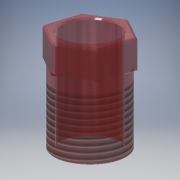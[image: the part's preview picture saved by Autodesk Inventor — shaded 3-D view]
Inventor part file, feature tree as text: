
AUTODESK INVENTOR PART (.ipt)
format: ipt  version: 2018 (Build 220112000, 112)  size: 318,464 bytes
history: native  units: mm
features: extrude x3, fillet x3, sketch x3, chamfer x1, thread x1
ambient origin geometry x8: Origin, YZ Plane, XZ Plane, XY Plane, X Axis, Y Axis, Z Axis, Center Point
bodies: Solid1 (feature_tree)
feature tree (11):
  extrude  "Extrusion1"  Depth=5.0mm TaperAngle=0.0deg
  extrude  "Extrusion2"  Depth=17.5mm TaperAngle=0.0deg
  extrude  "Extrusion3"  Depth=34.5mm TaperAngle=0.0deg
  chamfer  "Chamfer1"  Distance=0.25mm Angle=45.0deg
  thread  "Thread1"  [1 undecoded]
  fillet  "Fillet1"  Radius=0.5mm
  fillet  "Fillet2"  Radius=0.2mm
  fillet  "Fillet3"  Radius=0.2mm
  sketch  "Sketch1"  dims[d0=12.0mm d1=5.0mm d2=0.0mm]
  sketch  "Sketch2"  dims[d3=12.0mm d4=17.5mm d5=0.0mm]
  sketch  "Sketch3"  dims[d6=9.5mm d7=34.5mm d8=0.0mm d9=0.25mm d10=2.0mm d11=45.0deg d12=10.2mm d13=0.0mm d14=0.5mm d15=0.2mm d16=0.2mm]
note: 1 required parameter value undecoded (feature->parameter linkage not recoverable at this tier; creation-order binding heuristic only, values carry confidence <= 0.55)
